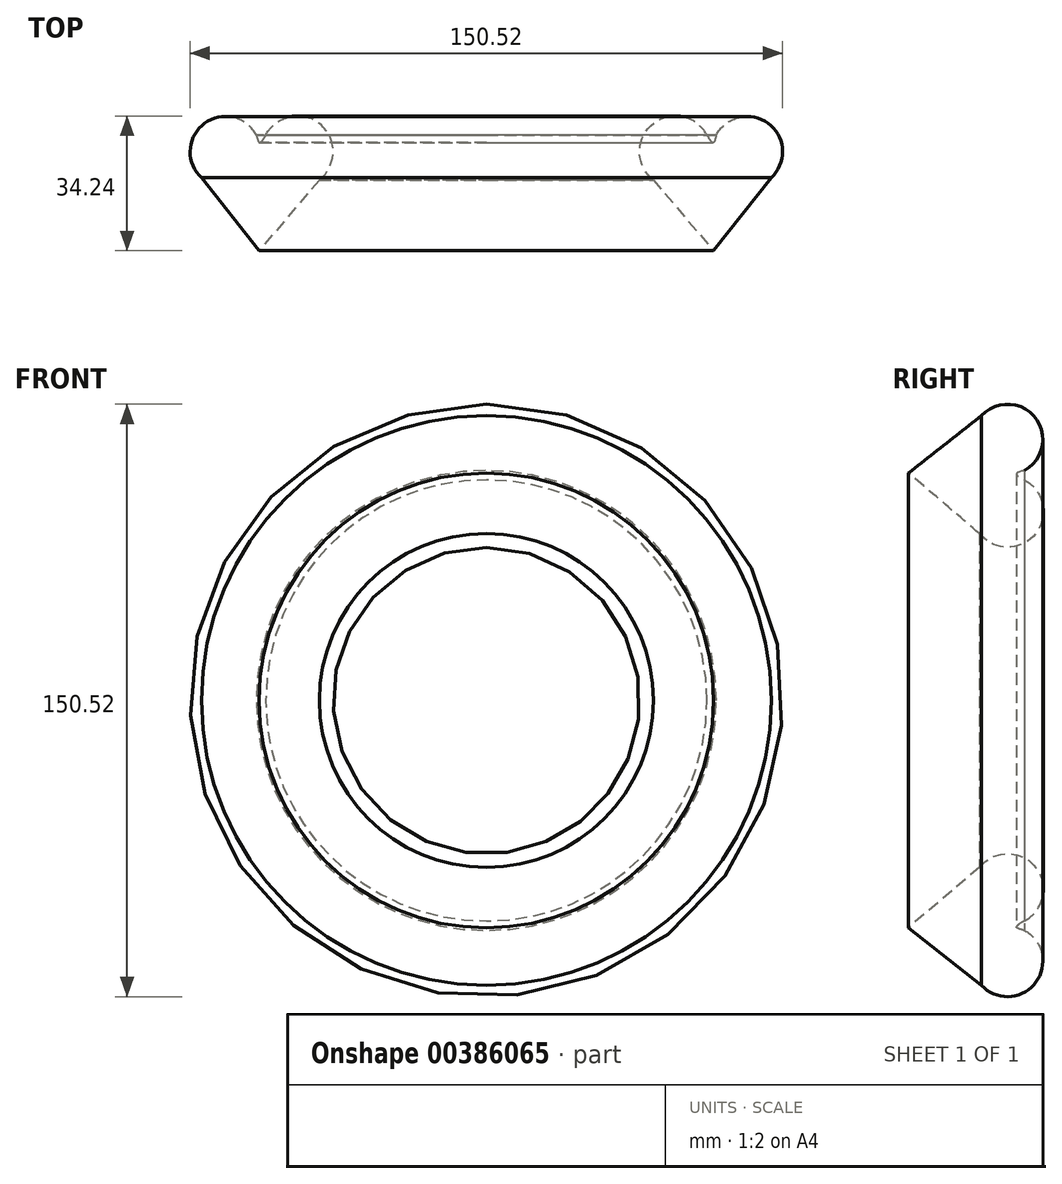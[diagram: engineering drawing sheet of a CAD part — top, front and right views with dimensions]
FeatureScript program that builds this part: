
annotation { "Feature Type Name" : "Feature", "Feature Type Description" : "" }
export const myFeature = defineFeature(function(context is Context, id is Id, definition is map)
    precondition{}
    {
        {
            var Q0;
            Q0=qCreatedBy(makeId("Top.planeOp"),FACE);
            var sketch = newSketch(context, id + "F0", { "sketchPlane" : qUnion([Q0])});
            skArc(sketch, "E0", {"start": v(-33.88, 29.43) * mm, "mid": v(-47.26, 32.22) * mm, "end": v(-47.84, 18.56) * mm});
            skArc(sketch, "E1", {"start": v(-17.9, 17.96) * mm, "mid": v(-17.6, 32.1) * mm, "end": v(-31.5, 29.43) * mm});
            skLineSegment(sketch, "E2", {"start": v(-49.58, 20.77) * mm, "end": v(-33.22, 0) * mm});
            skLineSegment(sketch, "E3", {"start": v(-15.5, 20.77) * mm, "end": v(-33.22, 0) * mm});
            skFitSpline(sketch, "E4", {"points": [v(-33.88, 29.43) * mm, v(-33.06, 27.44) * mm, v(-31.5, 29.43) * mm], "startDerivative": vector(1.41, -6.03) * mm, "endDerivative": vector(3.34, 5.87) * mm});
            skLineSegment(sketch, "E5", {"start": v(24.54, 35.2) * mm, "end": v(24.54, -36.77) * mm});
            skSolve(sketch);
        }
        {
            var Q0;
            {var subQ4=sQuery(id+"F0.wireOp",EDGE,"E4");Q0=makeQuery(id+"F0.imprint","IMPRINT",FACE,{"disambiguationData":[TD([[makeQuery(id+"F0.imprint","IMPRINT",EDGE,{"derivedFrom":subQ4}),-1.0]])]});}
            var Q1;
            {var subQ0=sQuery(id+"F0.wireOp",EDGE,"E2");var subQ1=sQuery(id+"F0.wireOp",EDGE,"E0");var subQ2=makeQuery(id+"F0.imprint","INTERSECT",VERTEX,{"disambiguationData":[OD(0.0)],"derivedFrom":[subQ1,subQ0]});Q1=makeQuery(id+"F0.imprint","IMPRINT",FACE,{"disambiguationData":[TD([[makeQuery(id+"F0.imprint","IMPRINT",EDGE,{"disambiguationData":[TD([[subQ2,1.0]])],"derivedFrom":subQ1}),1.0]])]});}
            var Q2;
            {var subQ0=sQuery(id+"F0.wireOp",EDGE,"E3");var subQ1=sQuery(id+"F0.wireOp",EDGE,"E1");var subQ2=makeQuery(id+"F0.imprint","INTERSECT",VERTEX,{"disambiguationData":[OD(0.0)],"derivedFrom":[subQ1,subQ0]});Q2=makeQuery(id+"F0.imprint","IMPRINT",FACE,{"disambiguationData":[TD([[makeQuery(id+"F0.imprint","IMPRINT",EDGE,{"disambiguationData":[TD([[subQ2,-1.0]])],"derivedFrom":subQ1}),1.0]])]});}
            var Q3;
            Q3=sQuery(id+"F0.wireOp",EDGE,"E5");
            revolve(context, id + "F1", {"entities" : qUnion([Q0, Q1, Q2]), "axis" : qUnion([Q3]), "revolveType" : RevolveType.FULL});
        }
    });
